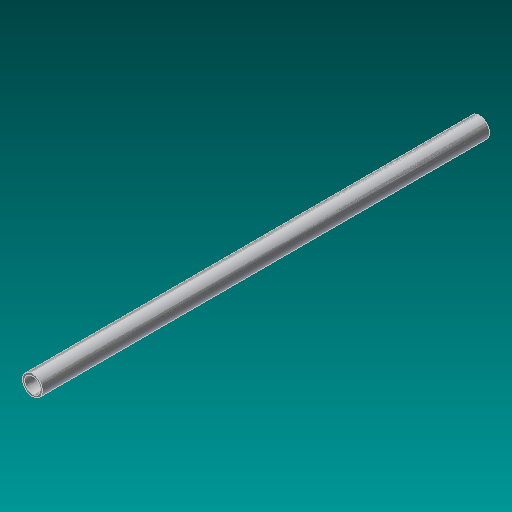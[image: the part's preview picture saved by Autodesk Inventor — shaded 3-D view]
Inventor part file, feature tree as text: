
AUTODESK INVENTOR PART (.ipt)
format: ipt  version: 2017 (Build 210142000, 142)  size: 97,280 bytes
history: native  units: in
note: dims shown in document units (in); Inventor stores cm internally (conversion verified against a paired STEP export)
features: extrude x1, sketch x1
ambient origin geometry x8: Origin, YZ Plane, XZ Plane, XY Plane, X Axis, Y Axis, Z Axis, Center Point
bodies: Solid1 (feature_tree)
feature tree (2):
  extrude  "Extrusion1"  Depth=42.25in
  sketch  "Sketch1"  dims[d0=1.9in d1=1.5in d2=42.25in d3=0.0in]
